AUTODESK INVENTOR PART (.ipt)
format: ipt  version: 2014 (Build 180170000, 170)  size: 885,248 bytes
history: native  units: in
note: dims shown in document units (in); Inventor stores cm internally (conversion verified against a paired STEP export)
features: sketch x8, plane x3, loft x2, extrude x2, fillet x2, other x1, imported_body x1
ambient origin geometry x8: Origin, YZ Plane, XZ Plane, XY Plane, X Axis, Y Axis, Z Axis, Center Point
bodies: Solid1 (feature_tree)
feature tree (19):
  other  "031-Fe_Bottom_Cover-0601-3_stp.ipt1"
  plane  "Work Plane1"
  sketch  "Sketch1"  dims[d0=0.3622in d1=0.5118in]
  plane  "Work Plane2"
  sketch  "Sketch2"  dims[d2=0.1575in d3=0.2362in]
  plane  "Work Plane3"
  loft  "Loft1"
  sketch  "Sketch4"  dims[d14=0.0in d15=90.0deg d16=0.0in d17=90.0deg]
  sketch  "Sketch5"  dims[d18=0.0in d19=90.0deg]
  sketch  "Sketch6"  dims[d20=0.0276in]
  extrude  "Extrusion1"  Depth=0.2362in
  loft  "Loft2"
  fillet  "Fillet1"  Radius=0.4331in
  fillet  "Fillet2"  Radius=0.315in
  extrude  "Extrusion2"  TaperAngle=0.0deg  [1 undecoded]
  imported_body  "Base1"
  sketch  "Sketch3"  dims[d4=0.0in d5=90.0deg d6=0.0in d7=90.0deg d8=0.0in d9=90.0deg d10=0.1575in d11=0.4331in d12=0.315in d13=-0.0137in]
  sketch  "Sketch7"  dims[d21=0.3937in]
  sketch  "Sketch8"  dims[d22=0.0197in d23=0.0in]
note: 1 required parameter value undecoded (feature->parameter linkage not recoverable at this tier; creation-order binding heuristic only, values carry confidence <= 0.55)
